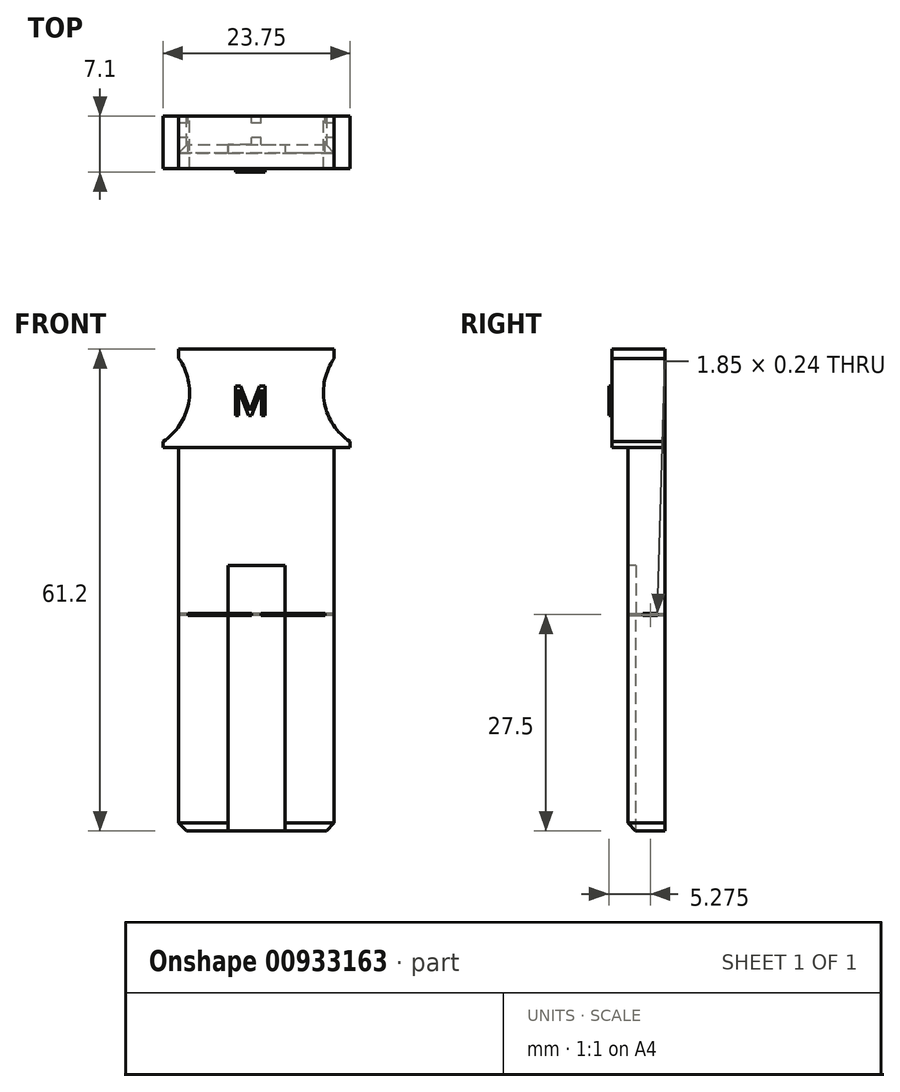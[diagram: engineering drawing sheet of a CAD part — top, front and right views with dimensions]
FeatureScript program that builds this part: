
annotation { "Feature Type Name" : "Feature", "Feature Type Description" : "" }
export const myFeature = defineFeature(function(context is Context, id is Id, definition is map)
    precondition{}
    {
        {
            var Q0;
            Q0=qCreatedBy(makeId("Front.planeOp"),FACE);
            var sketch = newSketch(context, id + "F0", { "sketchPlane" : qUnion([Q0])});
            skLineSegment(sketch, "E0.bottom", {"start": v(0, 0) * mm, "end": v(19.75, 0) * mm});
            skLineSegment(sketch, "E0.top", {"start": v(0, 61.2) * mm, "end": v(19.75, 61.2) * mm});
            skLineSegment(sketch, "E0.left", {"start": v(0, 0) * mm, "end": v(0, 61.2) * mm});
            skLineSegment(sketch, "E0.right", {"start": v(19.75, 0) * mm, "end": v(19.75, 61.2) * mm});
            skLineSegment(sketch, "E1", {"start": v(9.88, 61.2) * mm, "end": v(9.87, 0) * mm, "construction": true});
            skPoint(sketch, "E2", {"position": v(9.88, 34.73) * mm});
            skLineSegment(sketch, "E3", {"start": v(-7.67, 27.5) * mm, "end": v(34.9, 27.5) * mm, "construction": true});
            skLineSegment(sketch, "E4", {"start": v(0, 27.38) * mm, "end": v(0, 27.62) * mm});
            skCircle(sketch, "E5", {"center": v(25.88, 55.7) * mm, "radius": 7.5 * mm});
            skCircle(sketch, "E6.MirrorC", {"center": v(-6.13, 55.7) * mm, "radius": 7.5 * mm});
            skLineSegment(sketch, "E7.bottom", {"start": v(0, 27.62) * mm, "end": v(9.28, 27.62) * mm});
            skLineSegment(sketch, "E7.top", {"start": v(0, 27.62) * mm, "end": v(9.28, 27.62) * mm});
            skLineSegment(sketch, "E7.left", {"start": v(0, 27.62) * mm, "end": v(0, 27.62) * mm});
            skLineSegment(sketch, "E7.right", {"start": v(9.28, 27.62) * mm, "end": v(9.28, 27.62) * mm});
            skLineSegment(sketch, "E8", {"start": v(9.28, 27.62) * mm, "end": v(9.28, 27.38) * mm});
            skLineSegment(sketch, "E9", {"start": v(9.28, 27.38) * mm, "end": v(0, 27.38) * mm});
            skLineSegment(sketch, "E10", {"start": v(0, 27.62) * mm, "end": v(0, 27.38) * mm});
            skLineSegment(sketch, "E11.MirrorCS", {"start": v(19.75, 27.62) * mm, "end": v(10.48, 27.62) * mm});
            skLineSegment(sketch, "E12.MirrorCS", {"start": v(10.48, 27.62) * mm, "end": v(10.48, 27.38) * mm});
            skLineSegment(sketch, "E13.MirrorCS", {"start": v(10.48, 27.38) * mm, "end": v(19.75, 27.38) * mm});
            skLineSegment(sketch, "E14.MirrorCS", {"start": v(19.75, 27.62) * mm, "end": v(19.75, 27.38) * mm});
            skLineSegment(sketch, "E15.bottom", {"start": v(0, 48.7) * mm, "end": v(-2, 48.7) * mm});
            skLineSegment(sketch, "E15.top", {"start": v(0, 65.03) * mm, "end": v(-2, 65.03) * mm});
            skLineSegment(sketch, "E15.left", {"start": v(0, 48.7) * mm, "end": v(0, 65.03) * mm});
            skLineSegment(sketch, "E15.right", {"start": v(-2, 48.7) * mm, "end": v(-2, 65.03) * mm});
            skLineSegment(sketch, "E16.MirrorCS", {"start": v(19.75, 65.03) * mm, "end": v(21.75, 65.03) * mm});
            skLineSegment(sketch, "E17.MirrorCS", {"start": v(21.75, 48.7) * mm, "end": v(21.75, 65.03) * mm});
            skLineSegment(sketch, "E18.MirrorCS", {"start": v(19.75, 48.7) * mm, "end": v(21.75, 48.7) * mm});
            skLineSegment(sketch, "E19", {"start": v(1.2, 27.62) * mm, "end": v(1.2, 27.38) * mm});
            skLineSegment(sketch, "E20.MirrorCS", {"start": v(18.55, 27.62) * mm, "end": v(18.55, 27.38) * mm});
            skSolve(sketch);
        }
        {
            var Q0;
            {var subQ4=sQuery(id+"F0.wireOp",EDGE,"E0.bottom");Q0=makeQuery(id+"F0.imprint","IMPRINT",FACE,{"disambiguationData":[TD([[makeQuery(id+"F0.imprint","IMPRINT",EDGE,{"derivedFrom":subQ4}),1.0]])]});}
            var Q1;
            {var subQ0=sQuery(id+"F0.wireOp",EDGE,"E15.bottom");Q1=makeQuery(id+"F0.imprint","IMPRINT",FACE,{"disambiguationData":[TD([[makeQuery(id+"F0.imprint","IMPRINT",EDGE,{"derivedFrom":subQ0}),-1.0]])]});}
            var Q2;
            {var subQ0=sQuery(id+"F0.wireOp",EDGE,"E18.MirrorCS");Q2=makeQuery(id+"F0.imprint","IMPRINT",FACE,{"disambiguationData":[TD([[makeQuery(id+"F0.imprint","IMPRINT",EDGE,{"derivedFrom":subQ0}),1.0]])]});}
            var Q3;
            {var subQ5=sQuery(id+"F0.wireOp",EDGE,"E19");Q3=makeQuery(id+"F0.imprint","IMPRINT",FACE,{"disambiguationData":[TD([[makeQuery(id+"F0.imprint","IMPRINT",EDGE,{"derivedFrom":subQ5}),-1.0]])]});}
            var Q4;
            {var subQ5=sQuery(id+"F0.wireOp",EDGE,"E20.MirrorCS");Q4=makeQuery(id+"F0.imprint","IMPRINT",FACE,{"disambiguationData":[TD([[makeQuery(id+"F0.imprint","IMPRINT",EDGE,{"derivedFrom":subQ5}),1.0]])]});}
            extrude(context, id + "F1", {"entities" : qUnion([Q0, Q1, Q2, Q3, Q4]), "depth" : 4.7 * mm, "offsetDistance" : 25 * mm});
        }
        {
            var Q0;
            Q0=makeQuery(id+"F1.opExtrude","CAP_FACE",FACE,{"disambiguationData":[OSD([sQuery(id+"F0.wireOp",EDGE,"E0.bottom"),sQuery(id+"F0.wireOp",EDGE,"E0.top"),sQuery(id+"F0.wireOp",EDGE,"E0.left"),sQuery(id+"F0.wireOp",EDGE,"E0.right"),sQuery(id+"F0.wireOp",EDGE,"E5"),sQuery(id+"F0.wireOp",EDGE,"E6.MirrorC"),sQuery(id+"F0.wireOp",EDGE,"E7.bottom"),sQuery(id+"F0.wireOp",EDGE,"E8"),sQuery(id+"F0.wireOp",EDGE,"E9"),sQuery(id+"F0.wireOp",EDGE,"E11.MirrorCS"),sQuery(id+"F0.wireOp",EDGE,"E12.MirrorCS"),sQuery(id+"F0.wireOp",EDGE,"E13.MirrorCS"),sQuery(id+"F0.wireOp",EDGE,"E15.bottom"),sQuery(id+"F0.wireOp",EDGE,"E15.right"),sQuery(id+"F0.wireOp",EDGE,"E17.MirrorCS"),sQuery(id+"F0.wireOp",EDGE,"E18.MirrorCS"),sQuery(id+"F0.wireOp",EDGE,"E19"),sQuery(id+"F0.wireOp",EDGE,"E20.MirrorCS")])],"isStart":false});
            var sketch = newSketch(context, id + "F2", { "sketchPlane" : qUnion([Q0])});
            skLineSegment(sketch, "E21", {"start": v(6.28, 33.7) * mm, "end": v(13.48, 33.7) * mm});
            skLineSegment(sketch, "E22", {"start": v(13.48, 33.7) * mm, "end": v(13.48, 2.2) * mm});
            skLineSegment(sketch, "E23", {"start": v(13.48, 2.2) * mm, "end": v(13.48, 2.2) * mm});
            skLineSegment(sketch, "E24", {"start": v(13.48, 2.2) * mm, "end": v(13.48, 0) * mm});
            skLineSegment(sketch, "E25", {"start": v(13.48, 0) * mm, "end": v(6.28, 0) * mm});
            skLineSegment(sketch, "E26", {"start": v(6.28, 0) * mm, "end": v(6.28, 2.2) * mm});
            skLineSegment(sketch, "E27", {"start": v(6.28, 2.2) * mm, "end": v(6.28, 2.2) * mm});
            skLineSegment(sketch, "E28", {"start": v(6.28, 2.2) * mm, "end": v(6.28, 33.7) * mm});
            skLineSegment(sketch, "E29", {"start": v(9.88, 61.2) * mm, "end": v(9.88, 0) * mm, "construction": true});
            skSolve(sketch);
        }
        {
            var Q0;
            Q0=qSketchRegion(id+"F2",true);
            extrude(context, id + "F3", {"entities" : qUnion([Q0]), "operationType" : NewBodyOperationType.REMOVE, "oppositeDirection" : true, "depth" : 1.05 * mm, "offsetDistance" : 25 * mm});
        }
        {
            var Q0;
            {var subQ0=sQuery(id+"F0.wireOp",EDGE,"E0.right");Q0=makeQuery(id+"F1.opExtrude","SWEPT_FACE",FACE,{"disambiguationData":[OSD([subQ0]),TDD([makeQuery(id+"F0.imprint","IMPRINT",EDGE,{"disambiguationData":[TD([[makeQuery(id+"F0.imprint","INTERSECT",VERTEX,{"derivedFrom":[sQuery(id+"F0.wireOp",EDGE,"E0.top"),subQ0]}),1.0]])],"derivedFrom":subQ0})])]});}
            var sketch = newSketch(context, id + "F4", { "sketchPlane" : qUnion([Q0])});
            skLineSegment(sketch, "E30", {"start": v(-15.64, 31.3) * mm, "end": v(17.74, 31.3) * mm, "construction": true});
            skLineSegment(sketch, "E31", {"start": v(-1, 31.3) * mm, "end": v(0, 32.3) * mm});
            skLineSegment(sketch, "E32", {"start": v(0, 32.3) * mm, "end": v(0, 30.3) * mm});
            skLineSegment(sketch, "E33", {"start": v(0, 30.3) * mm, "end": v(-1, 31.3) * mm});
            skSolve(sketch);
        }
        {
            var Q0;
            Q0=makeQuery(id+"F1.opExtrude","CAP_FACE",FACE,{"disambiguationData":[OSD([sQuery(id+"F0.wireOp",EDGE,"E0.bottom"),sQuery(id+"F0.wireOp",EDGE,"E0.top"),sQuery(id+"F0.wireOp",EDGE,"E0.left"),sQuery(id+"F0.wireOp",EDGE,"E0.right"),sQuery(id+"F0.wireOp",EDGE,"E5"),sQuery(id+"F0.wireOp",EDGE,"E6.MirrorC"),sQuery(id+"F0.wireOp",EDGE,"E7.bottom"),sQuery(id+"F0.wireOp",EDGE,"E8"),sQuery(id+"F0.wireOp",EDGE,"E9"),sQuery(id+"F0.wireOp",EDGE,"E11.MirrorCS"),sQuery(id+"F0.wireOp",EDGE,"E12.MirrorCS"),sQuery(id+"F0.wireOp",EDGE,"E13.MirrorCS"),sQuery(id+"F0.wireOp",EDGE,"E15.bottom"),sQuery(id+"F0.wireOp",EDGE,"E15.right"),sQuery(id+"F0.wireOp",EDGE,"E17.MirrorCS"),sQuery(id+"F0.wireOp",EDGE,"E18.MirrorCS"),sQuery(id+"F0.wireOp",EDGE,"E19"),sQuery(id+"F0.wireOp",EDGE,"E20.MirrorCS")])],"isStart":false});
            var sketch = newSketch(context, id + "F5", { "sketchPlane" : qUnion([Q0])});
            skLineSegment(sketch, "E34", {"start": v(0, 48.7) * mm, "end": v(19.75, 48.7) * mm});
            skSolve(sketch);
        }
        {
            var Q0;
            Q0=makeQuery(id+"F5.imprint","IMPRINT",FACE,{"disambiguationData":[TD([[makeQuery(id+"F5.imprint","IMPRINT",EDGE,{"derivedFrom":sQuery(id+"F5.wireOp",EDGE,"E34")}),1.0]])]});
            extrude(context, id + "F6", {"entities" : qUnion([Q0]), "operationType" : NewBodyOperationType.ADD, "depth" : 2 * mm, "offsetDistance" : 25 * mm});
        }
        {
            var Q0;
            Q0=makeQuery(id+"F1.opExtrude","SWEPT_EDGE",EDGE,{"disambiguationData":[OSD([sQuery(id+"F0.wireOp",EDGE,"E0.bottom"),sQuery(id+"F0.wireOp",EDGE,"E0.left")])]});
            var Q1;
            Q1=makeQuery(id+"F1.opExtrude","SWEPT_EDGE",EDGE,{"disambiguationData":[OSD([sQuery(id+"F0.wireOp",EDGE,"E0.bottom"),sQuery(id+"F0.wireOp",EDGE,"E0.right")])]});
            var Q2;
            {var subQ0=sQuery(id+"F0.wireOp",EDGE,"E0.bottom");Q2=makeQuery(id+"F3.boolean.opBoolean","SPLIT",EDGE,{"disambiguationData":[TD([makeQuery(id+"F3.opExtrude","SWEPT_FACE",FACE,{"disambiguationData":[OSD([sQuery(id+"F2.wireOp",EDGE,"E26"),sQuery(id+"F2.wireOp",EDGE,"E28")])]})])],"derivedFrom":makeQuery(id+"F1.opExtrude","CAP_EDGE",EDGE,{"disambiguationData":[OSD([subQ0])],"isStart":false})});}
            var Q3;
            {var subQ0=sQuery(id+"F0.wireOp",EDGE,"E0.bottom");Q3=makeQuery(id+"F3.boolean.opBoolean","SPLIT",EDGE,{"disambiguationData":[TD([makeQuery(id+"F3.opExtrude","SWEPT_FACE",FACE,{"disambiguationData":[OSD([sQuery(id+"F2.wireOp",EDGE,"E22"),sQuery(id+"F2.wireOp",EDGE,"E24")])]})])],"derivedFrom":makeQuery(id+"F1.opExtrude","CAP_EDGE",EDGE,{"disambiguationData":[OSD([subQ0])],"isStart":false})});}
            var Q4;
            Q4=makeQuery(id+"F3.boolean.opBoolean","COPY",EDGE,{"derivedFrom":makeQuery(id+"F3.opExtrude","CAP_EDGE",EDGE,{"disambiguationData":[OSD([sQuery(id+"F2.wireOp",EDGE,"E25")])],"isStart":false})});
            chamfer(context, id + "F7", {"entities" : qUnion([Q0, Q1, Q2, Q3, Q4]), "width" : 1 * mm, "tangentPropagation" : true});
        }
        {
            var Q0;
            Q0=makeQuery(id+"F1.opExtrude","SWEPT_FACE",FACE,{"disambiguationData":[OSD([sQuery(id+"F0.wireOp",EDGE,"E8")])]});
            var sketch = newSketch(context, id + "F8", { "sketchPlane" : qUnion([Q0])});
            skLineSegment(sketch, "E35.bottom", {"start": v(0.9, 27.62) * mm, "end": v(2.75, 27.62) * mm});
            skLineSegment(sketch, "E35.top", {"start": v(0.9, 27.38) * mm, "end": v(2.75, 27.38) * mm});
            skLineSegment(sketch, "E35.left", {"start": v(0.9, 27.62) * mm, "end": v(0.9, 27.38) * mm});
            skLineSegment(sketch, "E35.right", {"start": v(2.75, 27.62) * mm, "end": v(2.75, 27.38) * mm});
            skLineSegment(sketch, "E36", {"start": v(0, 27.62) * mm, "end": v(0.9, 27.62) * mm, "construction": true});
            skLineSegment(sketch, "E37", {"start": v(2.75, 27.62) * mm, "end": v(3.65, 27.62) * mm, "construction": true});
            skSolve(sketch);
        }
        {
            var Q0;
            Q0=qSketchRegion(id+"F8",true);
            extrude(context, id + "F9", {"entities" : qUnion([Q0]), "operationType" : NewBodyOperationType.REMOVE, "endBound" : BoundingType.SYMMETRIC, "oppositeDirection" : true, "depth" : 250 * mm, "offsetDistance" : 25 * mm});
        }
        {
            var Q0;
            Q0=makeQuery(id+"F6.opExtrude","CAP_FACE",FACE,{"disambiguationData":[OSD([sQuery(id+"F0.wireOp",EDGE,"E0.top"),sQuery(id+"F0.wireOp",EDGE,"E0.left"),sQuery(id+"F0.wireOp",EDGE,"E0.right"),sQuery(id+"F0.wireOp",EDGE,"E5"),sQuery(id+"F0.wireOp",EDGE,"E6.MirrorC"),sQuery(id+"F0.wireOp",EDGE,"E15.bottom"),sQuery(id+"F0.wireOp",EDGE,"E15.right"),sQuery(id+"F0.wireOp",EDGE,"E17.MirrorCS"),sQuery(id+"F0.wireOp",EDGE,"E18.MirrorCS"),sQuery(id+"F5.wireOp",EDGE,"E34")])],"isStart":false});
            var sketch = newSketch(context, id + "F10", { "sketchPlane" : qUnion([Q0])});
            skText(sketch, "E38", { "text": "M", "fontName": "OpenSans-Regular.ttf"});
            const initialGuessF10  = {"E38": [0.00667, 0.05273, 1, 0, 0.00382]};
            skSetInitialGuess(sketch, initialGuessF10);
            skSolve(sketch);
        }
        {
            var Q0;
            Q0=qSketchRegion(id+"F10",true);
            extrude(context, id + "F11", {"entities" : qUnion([Q0]), "operationType" : NewBodyOperationType.ADD, "depth" : 0.4 * mm, "offsetDistance" : 25 * mm});
        }
    });
